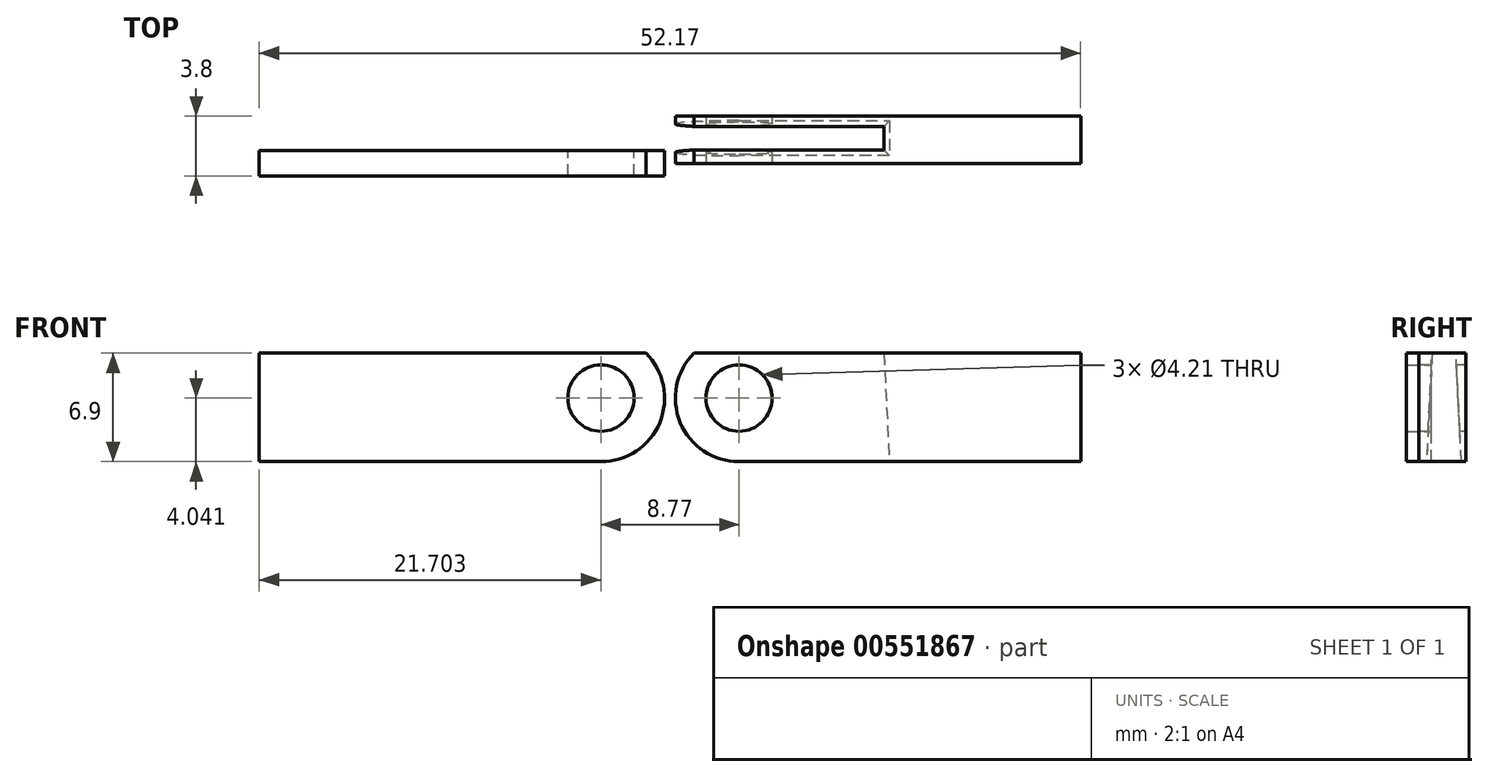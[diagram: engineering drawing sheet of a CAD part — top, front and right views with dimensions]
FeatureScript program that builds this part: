
annotation { "Feature Type Name" : "Feature", "Feature Type Description" : "" }
export const myFeature = defineFeature(function(context is Context, id is Id, definition is map)
    precondition{}
    {
        {
            var Q0;
            Q0=qCreatedBy(makeId("Front.planeOp"),FACE);
            var sketch = newSketch(context, id + "F0", { "sketchPlane" : qUnion([Q0])});
            skLineSegment(sketch, "E0.bottom", {"start": v(-4.42, 0) * mm, "end": v(17.28, 0) * mm});
            skLineSegment(sketch, "E0.right", {"start": v(17.28, 0) * mm, "end": v(17.28, 6.9) * mm});
            skArc(sketch, "E1", {"start": v(-7.27, 6.9) * mm, "mid": v(-8.15, 2.5) * mm, "end": v(-4.42, 0) * mm});
            skCircle(sketch, "E2", {"center": v(-4.42, 4.04) * mm, "radius": 2.1 * mm});
            skLineSegment(sketch, "E3", {"start": v(-1.12, 6.9) * mm, "end": v(17.28, 6.9) * mm});
            skLineSegment(sketch, "E4.MirrorCS", {"start": v(-16.48, 6.9) * mm, "end": v(-34.89, 6.9) * mm});
            skLineSegment(sketch, "E5.MirrorCS", {"start": v(-34.89, 0) * mm, "end": v(-34.89, 6.9) * mm});
            skLineSegment(sketch, "E6.MirrorCS", {"start": v(-13.19, 0) * mm, "end": v(-34.89, 0) * mm});
            skCircle(sketch, "E7.MirrorC", {"center": v(-13.19, 4.04) * mm, "radius": 2.1 * mm});
            skArc(sketch, "E8.MirrorCS", {"start": v(-10.34, 6.9) * mm, "mid": v(-9.45, 2.5) * mm, "end": v(-13.19, 0) * mm});
            skCircle(sketch, "E9", {"center": v(-4.42, 4.04) * mm, "radius": 2.07 * mm});
            skLineSegment(sketch, "E10", {"start": v(-16.48, 6.9) * mm, "end": v(-10.34, 6.9) * mm});
            skLineSegment(sketch, "E11", {"start": v(-1.12, 6.9) * mm, "end": v(-7.27, 6.9) * mm});
            skPoint(sketch, "E12.MirrorCS.end.orphan", {"position": v(-16.48, 8.08) * mm});
            skPoint(sketch, "E13.orphan", {"position": v(-13.19, 8.08) * mm});
            skPoint(sketch, "E0.top.start.orphan", {"position": v(-4.42, 8.08) * mm});
            skPoint(sketch, "E14.start.orphan", {"position": v(-1.12, 8.08) * mm});
            skSolve(sketch);
        }
        {
            var Q0;
            Q0=makeQuery(id+"F0.imprint","IMPRINT",FACE,{"disambiguationData":[TD([[makeQuery(id+"F0.imprint","IMPRINT",EDGE,{"derivedFrom":sQuery(id+"F0.wireOp",EDGE,"E0.bottom")}),1.0]])]});
            extrude(context, id + "F1", {"entities" : qUnion([Q0]), "oppositeDirection" : true, "depth" : 3 * mm, "offsetDistance" : 25 * mm});
        }
        {
            var Q0;
            Q0=makeQuery(id+"F1.opExtrude","SWEPT_FACE",FACE,{"disambiguationData":[OSD([sQuery(id+"F0.wireOp",EDGE,"E3")])]});
            var sketch = newSketch(context, id + "F2", { "sketchPlane" : qUnion([Q0])});
            skLineSegment(sketch, "E15.bottom", {"start": v(-9.98, 2.35) * mm, "end": v(4.78, 2.35) * mm});
            skLineSegment(sketch, "E15.top", {"start": v(-9.98, 0.85) * mm, "end": v(4.78, 0.85) * mm});
            skLineSegment(sketch, "E15.left", {"start": v(-9.98, 2.35) * mm, "end": v(-9.98, 0.85) * mm});
            skLineSegment(sketch, "E15.right", {"start": v(4.78, 2.35) * mm, "end": v(4.78, 0.85) * mm});
            skSolve(sketch);
        }
        {
            var Q0;
            Q0 = qSketchRegion(id + "F2", true);
            extrude(context, id + "F3", {"entities" : qUnion([Q0]), "operationType" : NewBodyOperationType.REMOVE, "endBound" : BoundingType.SYMMETRIC, "oppositeDirection" : true, "depth" : 25 * mm, "offsetDistance" : 25 * mm, "hasDraft" : true, "draftAngle" : 3 * degree});
        }
        {
            var Q0;
            Q0=makeQuery(id+"F0.imprint","IMPRINT",FACE,{"disambiguationData":[TD([[makeQuery(id+"F0.imprint","IMPRINT",EDGE,{"derivedFrom":sQuery(id+"F0.wireOp",EDGE,"E4.MirrorCS")}),1.0]])]});
            extrude(context, id + "F4", {"entities" : qUnion([Q0]), "endBound" : BoundingType.SYMMETRIC, "depth" : 1.6 * mm, "offsetDistance" : 25 * mm});
        }
    });
